# Revit family: ВЦУ_Eng
name_source: partatom
category: Mechanical Equipment
units: mm (PartAtom-declared; Revit-internal decimal feet)

## family parameters
Always vertical = Yes
Classification = None
Cut with Voids When Loaded = No
Part Type = Normal
Room Calculation Point = No
Round Connector Dimension = Use Diameter
Shared = No
Work Plane-Based = No

## types (8) — shared parameters
00_20_Manufacturer = Vents
00_20_Name = Scroll-type single-inlet centrifugal fan
Casing Material = Metal, painted, blue, matte RAL 5007
Description = One-sided suction
Direction = No
F = 30 mm  [stored 0.0984252 ft]
Frequency = 50 Hz
Load Classification = HVAC
Maintenance zone material = <By Category>
Manufacturer = Vents
Number of Fase = 1
URL = https://ventilation-system.com
Voltage = 230 V
r = 2 mm  [stored 0.00656168 ft]
r1 = 10 mm  [stored 0.0328084 ft]
t = 2 mm  [stored 0.00656168 ft]
zero-valued in all types: Default Elevation

## per-type parameters (varying)
- VCU 2E 140х60: Amperage=1 A; Apparent Load=147 VA; B=243 mm; D=140 mm; D1=200 mm; Diameter=140 mm; E=0 mm  [stored 0 ft]; H=287 mm; H1=125 mm; H2=93 mm; Height=287 mm; L=86 mm  [stored 0.282152 ft]; L1=110 mm; L2=78 mm  [stored 0.255906 ft]; Length=243 mm; M=150 mm; M1=200 mm; M2=100 mm; M3=90 mm  [stored 0.295276 ft]; Maximum Air Flow=515.0 m³/h; P=116 mm; Power=148 W; R=70 mm  [stored 0.229659 ft]; R1=100 mm; R2=85 mm  [stored 0.278871 ft]; R3=35 mm  [stored 0.114829 ft]; Sound pressure level at 3 m distance=68 dBA; Temperature of moving air=-25...+45 °С; Weight=3.70 kg; Width=138 mm; d=9 mm  [stored 0.0295276 ft]; d1=110 mm; d2=105 mm; d3=320 mm; h1=70 mm  [stored 0.229659 ft]; h2=40 mm  [stored 0.131234 ft]; h22=46 mm; h222=48 mm; h3=90 mm  [stored 0.295276 ft]; l=82 mm  [stored 0.269029 ft]; l1=43 mm  [stored 0.141076 ft]; ln=45 mm  [stored 0.147638 ft]
- VCU 4E 250х140: Amperage=2 A; Apparent Load=570 VA; B=410 mm; D=250 mm; D1=310 mm; Diameter=250 mm; E=8 mm  [stored 0.0262467 ft]; H=485 mm; H1=230 mm; H2=191 mm; Height=485 mm; L=205 mm; L1=230 mm; L2=197 mm; Length=410 mm; M=270 mm; M1=320 mm; M2=160 mm; M3=150 mm; Maximum Air Flow=2000.0 m³/h; P=238 mm; Power=570 W; R=125 mm; R1=155 mm; R2=140 mm; R3=63 mm  [stored 0.206693 ft]; Sound pressure level at 3 m distance=60 dBA; Temperature of moving air=-40...+70 °С; Weight=16.30 kg; Width=260 mm; d=11 mm  [stored 0.0360892 ft]; d1=170 mm; d2=165 mm; d3=440 mm; h1=123 mm; h2=93 mm; h22=96 mm; h222=98 mm; h3=145 mm; l=201 mm; l1=103 mm; ln=105 mm
- VCU 2E 160х62: Amperage=1 A; Apparent Load=269 VA; B=277 mm; D=160 mm; D1=220 mm; Diameter=160 mm; E=3 mm  [stored 0.00984252 ft]; H=324 mm; H1=136 mm; H2=106 mm; Height=324 mm; L=106 mm; L1=130 mm; L2=98 mm; Length=277 mm; M=200 mm; M1=250 mm; M2=125 mm; M3=115 mm; Maximum Air Flow=560.0 m³/h; P=139 mm; Power=264 W; R=80 mm  [stored 0.262467 ft]; R1=110 mm; R2=95 mm; R3=40 mm  [stored 0.131234 ft]; Sound pressure level at 3 m distance=70 dBA; Temperature of moving air=-25...+50 °С; Weight=4.80 kg; Width=161 mm; d=9 mm  [stored 0.0295276 ft]; d1=115 mm; d2=110 mm; d3=330 mm; h1=76 mm  [stored 0.249344 ft]; h2=46 mm; h22=53 mm  [stored 0.173885 ft]; h222=55 mm  [stored 0.180446 ft]; h3=100 mm; l=102 mm; l1=53 mm  [stored 0.173885 ft]; ln=55 mm  [stored 0.180446 ft]
- VCU 4E 180х92: Amperage=1 A; Apparent Load=161 VA; B=311 mm; D=180 mm; D1=240 mm; Diameter=180 mm; E=7 mm  [stored 0.0229659 ft]; H=360 mm; H1=150 mm; H2=120 mm; Height=360 mm; L=148 mm; L1=170 mm; L2=140 mm; Length=311 mm; M=230 mm; M1=280 mm; M2=140 mm; M3=130 mm; Maximum Air Flow=800.0 m³/h; P=181 mm; Power=160 W; R=90 mm  [stored 0.295276 ft]; R1=120 mm; R2=105 mm; R3=45 mm  [stored 0.147638 ft]; Sound pressure level at 3 m distance=62 dBA; Temperature of moving air=-25...+45 °С; Weight=7.10 kg; Width=203 mm; d=9 mm  [stored 0.0295276 ft]; d1=125 mm; d2=120 mm; d3=350 mm; h1=83 mm; h2=53 mm  [stored 0.173885 ft]; h22=60 mm  [stored 0.19685 ft]; h222=62 mm  [stored 0.203412 ft]; h3=110 mm; l=144 mm; l1=74 mm  [stored 0.242782 ft]; ln=76 mm  [stored 0.249344 ft]
- VCU 4E 200х80: Amperage=1 A; Apparent Load=127 VA; B=345 mm; D=200 mm; D1=260 mm; Diameter=200 mm; E=8 mm  [stored 0.0262467 ft]; H=398 mm; H1=165 mm; H2=134 mm; Height=398 mm; L=116 mm; L1=140 mm; L2=108 mm; Length=345 mm; M=240 mm; M1=290 mm; M2=145 mm; M3=135 mm; Maximum Air Flow=730.0 m³/h; P=150 mm; Power=125 W; R=100 mm; R1=130 mm; R2=115 mm; R3=50 mm  [stored 0.164042 ft]; Sound pressure level at 3 m distance=63 dBA; Temperature of moving air=-25...+45 °С; Weight=7.50 kg; Width=172 mm; d=9 mm  [stored 0.0295276 ft]; d1=138 mm; d2=133 mm; d3=375 mm; h1=90 mm  [stored 0.295276 ft]; h2=60 mm  [stored 0.19685 ft]; h22=67 mm; h222=69 mm  [stored 0.226378 ft]; h3=120 mm; l=112 mm; l1=58 mm  [stored 0.190289 ft]; ln=60 mm  [stored 0.19685 ft]
- VCU 4E 200х102: Amperage=1 A; Apparent Load=288 VA; B=345 mm; D=200 mm; D1=260 mm; Diameter=200 mm; E=8 mm  [stored 0.0262467 ft]; H=398 mm; H1=165 mm; H2=134 mm; Height=398 mm; L=152 mm; L1=175 mm; L2=143 mm; Length=345 mm; M=240 mm; M1=290 mm; M2=145 mm; M3=135 mm; Maximum Air Flow=1350.0 m³/h; P=185 mm; Power=280 W; R=100 mm; R1=130 mm; R2=115 mm; R3=50 mm  [stored 0.164042 ft]; Sound pressure level at 3 m distance=65 dBA; Temperature of moving air=-25...+40 °С; Weight=8.00 kg; Width=207 mm; d=9 mm  [stored 0.0295276 ft]; d1=138 mm; d2=133 mm; d3=375 mm; h1=90 mm  [stored 0.295276 ft]; h2=60 mm  [stored 0.19685 ft]; h22=67 mm; h222=69 mm  [stored 0.226378 ft]; h3=120 mm; l=148 mm; l1=76 mm  [stored 0.249344 ft]; ln=78 mm  [stored 0.255906 ft]
- VCU 4E 225х102: Amperage=2 A; Apparent Load=455 VA; B=365 mm; D=225 mm; D1=285 mm; Diameter=225 mm; E=5 mm  [stored 0.0164042 ft]; H=441 mm; H1=210 mm; H2=171 mm; Height=441 mm; L=145 mm; L1=170 mm; L2=137 mm; Length=365 mm; M=250 mm; M1=300 mm; M2=150 mm; M3=140 mm; Maximum Air Flow=1480.0 m³/h; P=178 mm; Power=395 W; R=113 mm; R1=143 mm; R2=128 mm; R3=56 mm  [stored 0.183727 ft]; Sound pressure level at 3 m distance=69 dBA; Temperature of moving air=-40...+70 °С; Weight=11.90 kg; Width=200 mm; d=11 mm  [stored 0.0360892 ft]; d1=150 mm; d2=145 mm; d3=400 mm; h1=113 mm; h2=83 mm; h22=86 mm  [stored 0.282152 ft]; h222=88 mm; h3=133 mm; l=141 mm; l1=73 mm; ln=75 mm  [stored 0.246063 ft]
- VCU 4E 250х102: Amperage=4 A; Apparent Load=840 VA; B=410 mm; D=250 mm; D1=310 mm; Diameter=250 mm; E=8 mm  [stored 0.0262467 ft]; H=485 mm; H1=230 mm; H2=191 mm; Height=485 mm; L=165 mm; L1=190 mm; L2=157 mm; Length=410 mm; M=270 mm; M1=320 mm; M2=160 mm; M3=150 mm; Maximum Air Flow=2000.0 m³/h; P=198 mm; Power=810 W; R=125 mm; R1=155 mm; R2=140 mm; R3=63 mm  [stored 0.206693 ft]; Sound pressure level at 3 m distance=63 dBA; Temperature of moving air=-40...+70 °С; Weight=16.30 kg; Width=220 mm; d=11 mm  [stored 0.0360892 ft]; d1=170 mm; d2=165 mm; d3=440 mm; h1=123 mm; h2=93 mm; h22=96 mm; h222=98 mm; h3=145 mm; l=161 mm; l1=83 mm; ln=85 mm  [stored 0.278871 ft]

note: column(s) folded — value = type name in every type: 00_20_Type

note: [stored X ft] marks values corroborated as IEEE doubles in the binary element streams (Revit-internal decimal feet)
